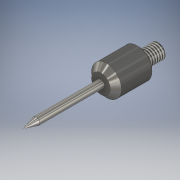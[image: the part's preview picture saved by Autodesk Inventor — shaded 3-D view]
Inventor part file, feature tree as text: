
AUTODESK INVENTOR PART (.ipt)
format: ipt  version: 2016 SP1 (Build 200210100, 210)  size: 148,992 bytes
history: native  units: in
note: dims shown in document units (in); Inventor stores cm internally (conversion verified against a paired STEP export)
features: chamfer x2, sketch x2, revolve x1, extrude x1, thread x1, projected_geometry x1
ambient origin geometry x8: Origin, YZ Plane, XZ Plane, XY Plane, X Axis, Y Axis, Z Axis, Center Point
bodies: Solid1 (feature_tree)
feature tree (8):
  revolve  "Revolution1"  [1 undecoded]
  extrude  "Extrusion1"  Depth=0.52in
  chamfer  "Chamfer1"  Angle=90.0deg  [1 undecoded]
  chamfer  "Chamfer2"  Distance=0.1181in
  thread  "Thread1"  [1 undecoded]
  sketch  "Sketch1"  dims[d0=0.1201in d1=0.3in]
  sketch  "Sketch2"  dims[d2=0.03in d3=0.52in d4=90.0deg d5=0.1181in d6=0.1575in d7=0.0in d8=0.045in d9=0.125in d10=45.0deg d11=1.0in d12=0.0in d13=75.0deg d14=15.0deg d15=0.632in d16=0.932in d17=0.01in d18=0.125in d19=45.0deg]
  projected_geometry  "Projected Loop1"
note: 3 required parameter values undecoded (feature->parameter linkage not recoverable at this tier; creation-order binding heuristic only, values carry confidence <= 0.55)